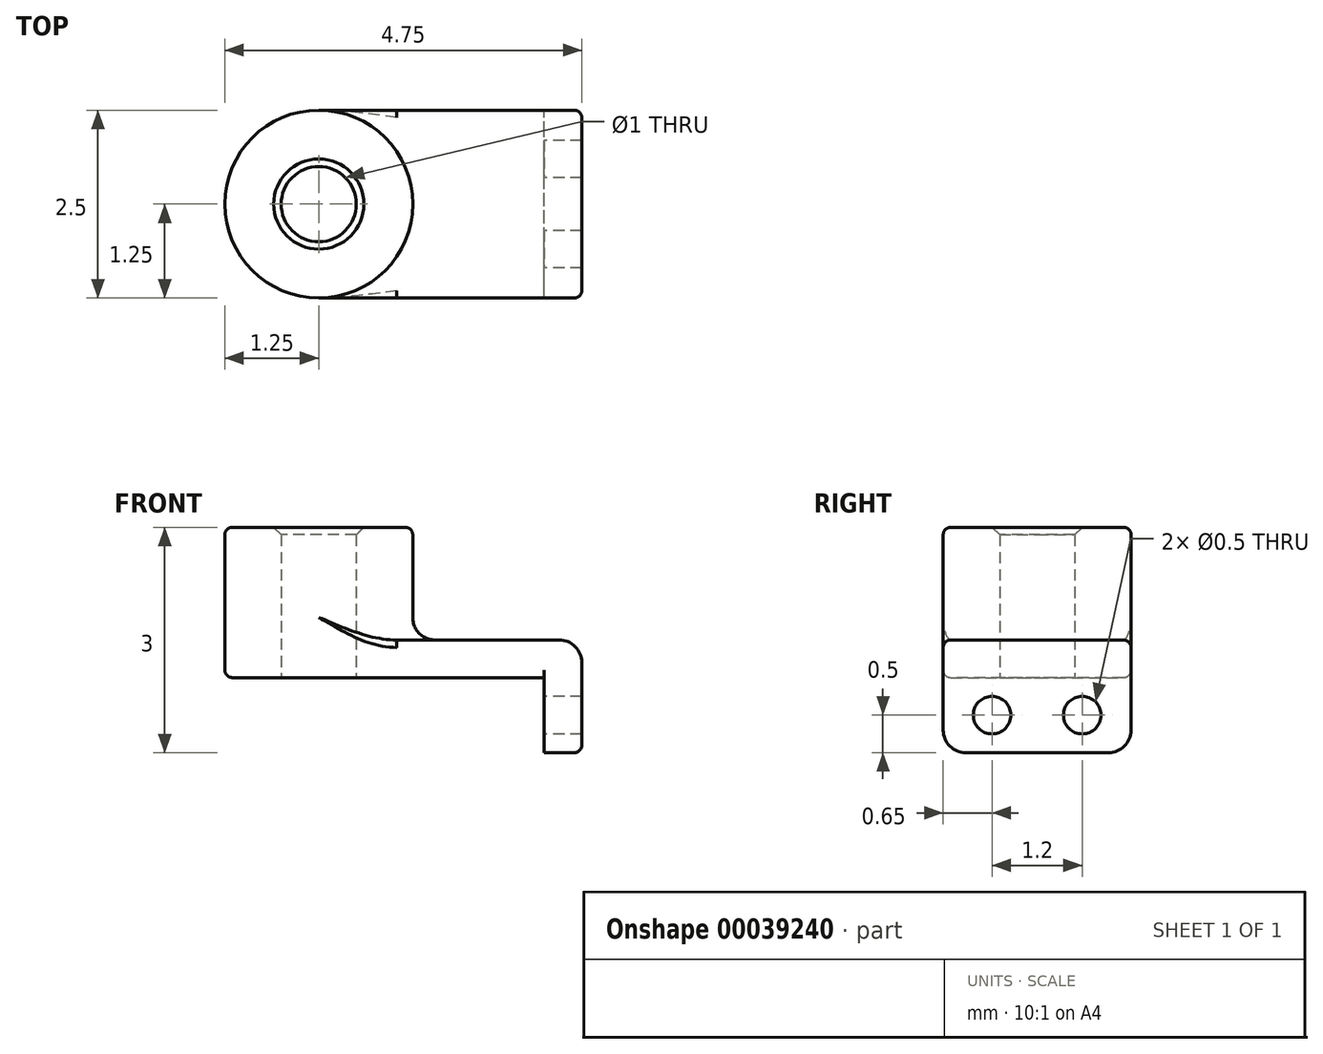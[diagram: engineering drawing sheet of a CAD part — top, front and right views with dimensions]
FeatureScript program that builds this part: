
annotation { "Feature Type Name" : "Feature", "Feature Type Description" : "" }
export const myFeature = defineFeature(function(context is Context, id is Id, definition is map)
    precondition{}
    {
        {
            var Q0;
            Q0=qCreatedBy(makeId("Top.planeOp"),FACE);
            var sketch = newSketch(context, id + "F0", { "sketchPlane" : qUnion([Q0])});
            skLineSegment(sketch, "E0.rect.bottom", {"start": v(1.5, -1.25) * mm, "end": v(-1.5, -1.25) * mm});
            skLineSegment(sketch, "E0.rect.top", {"start": v(1.5, 1.25) * mm, "end": v(-1.5, 1.25) * mm});
            skLineSegment(sketch, "E0.rect.left", {"start": v(1.5, -1.25) * mm, "end": v(1.5, 1.25) * mm});
            skLineSegment(sketch, "E0.rect.right", {"start": v(-1.5, -1.25) * mm, "end": v(-1.5, 1.25) * mm});
            skPoint(sketch, "E0.rect.middle", {"position": v(0, 0) * mm});
            skCircle(sketch, "E1", {"center": v(-1.5, 0) * mm, "radius": 1.25 * mm});
            skCircle(sketch, "E2", {"center": v(-1.5, 0) * mm, "radius": 0.5 * mm});
            skSolve(sketch);
        }
        {
            var Q0;
            {var subQ3=sQuery(id+"F0.wireOp",EDGE,"E0.rect.bottom");Q0=makeQuery(id+"F0.imprint","IMPRINT",FACE,{"disambiguationData":[TD([[makeQuery(id+"F0.imprint","IMPRINT",EDGE,{"derivedFrom":subQ3}),-1.0]])]});}
            var Q1;
            {var subQ0=sQuery(id+"F0.wireOp",EDGE,"E2");var subQ1=sQuery(id+"F0.wireOp",EDGE,"E0.rect.right");var subQ3=makeQuery(id+"F0.imprint","INTERSECT",VERTEX,{"disambiguationData":[OD(0.0)],"derivedFrom":[subQ1,subQ0]});Q1=makeQuery(id+"F0.imprint","IMPRINT",FACE,{"disambiguationData":[TD([[makeQuery(id+"F0.imprint","IMPRINT",EDGE,{"disambiguationData":[TD([[subQ3,-1.0]])],"derivedFrom":subQ0}),-1.0]])]});}
            var Q2;
            {var subQ0=sQuery(id+"F0.wireOp",EDGE,"E2");var subQ1=sQuery(id+"F0.wireOp",EDGE,"E0.rect.right");var subQ3=makeQuery(id+"F0.imprint","INTERSECT",VERTEX,{"disambiguationData":[OD(0.0)],"derivedFrom":[subQ1,subQ0]});Q2=makeQuery(id+"F0.imprint","IMPRINT",FACE,{"disambiguationData":[TD([[makeQuery(id+"F0.imprint","IMPRINT",EDGE,{"disambiguationData":[TD([[subQ3,1.0]])],"derivedFrom":subQ0}),-1.0]])]});}
            extrude(context, id + "F1", {"entities" : qUnion([Q0, Q1, Q2]), "depth" : .5 * mm});
        }
        {
            var Q0;
            {var subQ0=sQuery(id+"F0.wireOp",EDGE,"E2");var subQ1=sQuery(id+"F0.wireOp",EDGE,"E0.rect.right");var subQ3=makeQuery(id+"F0.imprint","INTERSECT",VERTEX,{"disambiguationData":[OD(0.0)],"derivedFrom":[subQ1,subQ0]});Q0=makeQuery(id+"F0.imprint","IMPRINT",FACE,{"disambiguationData":[TD([[makeQuery(id+"F0.imprint","IMPRINT",EDGE,{"disambiguationData":[TD([[subQ3,-1.0]])],"derivedFrom":subQ0}),-1.0]])]});}
            var Q1;
            {var subQ0=sQuery(id+"F0.wireOp",EDGE,"E2");var subQ1=sQuery(id+"F0.wireOp",EDGE,"E0.rect.right");var subQ3=makeQuery(id+"F0.imprint","INTERSECT",VERTEX,{"disambiguationData":[OD(0.0)],"derivedFrom":[subQ1,subQ0]});Q1=makeQuery(id+"F0.imprint","IMPRINT",FACE,{"disambiguationData":[TD([[makeQuery(id+"F0.imprint","IMPRINT",EDGE,{"disambiguationData":[TD([[subQ3,1.0]])],"derivedFrom":subQ0}),-1.0]])]});}
            extrude(context, id + "F2", {"entities" : qUnion([Q0, Q1]), "operationType" : NewBodyOperationType.ADD, "depth" : 2 * mm});
        }
        {
            var Q0;
            Q0=makeQuery(id+"F1.opExtrude","SWEPT_FACE",FACE,{"disambiguationData":[OSD([sQuery(id+"F0.wireOp",EDGE,"E0.rect.left")])]});
            var sketch = newSketch(context, id + "F3", { "sketchPlane" : qUnion([Q0])});
            skLineSegment(sketch, "E3.bottom", {"start": v(-1.25, 0.5) * mm, "end": v(1.25, 0.5) * mm});
            skLineSegment(sketch, "E3.top", {"start": v(-1.25, -1) * mm, "end": v(1.25, -1) * mm});
            skLineSegment(sketch, "E3.left", {"start": v(-1.25, 0.5) * mm, "end": v(-1.25, -1) * mm});
            skLineSegment(sketch, "E3.right", {"start": v(1.25, 0.5) * mm, "end": v(1.25, -1) * mm});
            skLineSegment(sketch, "E4", {"start": v(0, 0) * mm, "end": v(0, -1) * mm, "construction": true});
            skCircle(sketch, "E5", {"center": v(-0.6, -0.5) * mm, "radius": 0.25 * mm});
            skCircle(sketch, "E6.MirrorC", {"center": v(0.6, -0.5) * mm, "radius": 0.25 * mm});
            skSolve(sketch);
        }
        {
            var Q0;
            Q0 = qSketchRegion(id + "F3", true);
            extrude(context, id + "F4", {"entities" : qUnion([Q0]), "operationType" : NewBodyOperationType.ADD, "depth" : .5 * mm});
        }
        {
            var Q0;
            {var subQ0=sQuery(id+"F0.wireOp",EDGE,"E1");Q0=makeQuery(id+"F2.boolean.opBoolean","INTERSECT",EDGE,{"derivedFrom":[makeQuery(id+"F1.opExtrude","CAP_FACE",FACE,{"disambiguationData":[OSD([sQuery(id+"F0.wireOp",EDGE,"E0.rect.bottom"),sQuery(id+"F0.wireOp",EDGE,"E0.rect.top"),sQuery(id+"F0.wireOp",EDGE,"E0.rect.left"),subQ0,sQuery(id+"F0.wireOp",EDGE,"E2")])],"isStart":false}),makeQuery(id+"F2.opExtrude","SWEPT_FACE",FACE,{"disambiguationData":[OSD([subQ0])]})]});}
            var Q1;
            Q1=makeQuery(id+"F4.opExtrude","SWEPT_EDGE",EDGE,{"disambiguationData":[OSD([sQuery(id+"F3.wireOp",EDGE,"E3.top"),sQuery(id+"F3.wireOp",EDGE,"E3.left")])]});
            var Q2;
            Q2=makeQuery(id+"F4.opExtrude","SWEPT_EDGE",EDGE,{"disambiguationData":[OSD([sQuery(id+"F3.wireOp",EDGE,"E3.top"),sQuery(id+"F3.wireOp",EDGE,"E3.right")])]});
            var Q3;
            Q3=makeQuery(id+"F1.opExtrude","CAP_EDGE",EDGE,{"disambiguationData":[OSD([sQuery(id+"F0.wireOp",EDGE,"E0.rect.left")])],"isStart":true});
            var Q4;
            Q4=makeQuery(id+"F4.opExtrude","CAP_EDGE",EDGE,{"disambiguationData":[OSD([sQuery(id+"F3.wireOp",EDGE,"E3.bottom")])],"isStart":false});
            fillet(context, id + "F5", {"entities" : qUnion([Q0, Q1, Q2, Q3, Q4]), "radius" : .3 * mm, "tangentPropagation" : true, "allowEdgeOverflow" : false});
        }
        {
            var Q0;
            Q0=makeQuery(id+"F4.boolean.opBoolean","MERGE",EDGE,{"derivedFrom":[makeQuery(id+"F1.opExtrude","CAP_EDGE",EDGE,{"disambiguationData":[OSD([sQuery(id+"F0.wireOp",EDGE,"E0.rect.bottom")])],"isStart":false}),makeQuery(id+"F4.opExtrude","SWEPT_EDGE",EDGE,{"disambiguationData":[OSD([sQuery(id+"F3.wireOp",EDGE,"E3.bottom"),sQuery(id+"F3.wireOp",EDGE,"E3.left")])]})]});
            var Q1;
            Q1=makeQuery(id+"F1.opExtrude","CAP_EDGE",EDGE,{"disambiguationData":[OSD([sQuery(id+"F0.wireOp",EDGE,"E0.rect.bottom")])],"isStart":true});
            var Q2;
            Q2=makeQuery(id+"F2.opExtrude","CAP_EDGE",EDGE,{"disambiguationData":[OSD([sQuery(id+"F0.wireOp",EDGE,"E1")])],"isStart":false});
            fillet(context, id + "F6", {"entities" : qUnion([Q0, Q1, Q2]), "radius" : .1 * mm, "tangentPropagation" : true, "allowEdgeOverflow" : false});
        }
        {
            var Q0;
            Q0=makeQuery(id+"F2.opExtrude","CAP_EDGE",EDGE,{"disambiguationData":[OSD([sQuery(id+"F0.wireOp",EDGE,"E2")])],"isStart":false});
            chamfer(context, id + "F7", {"entities" : qUnion([Q0]), "width" : .1 * mm, "tangentPropagation" : true});
        }
    });
